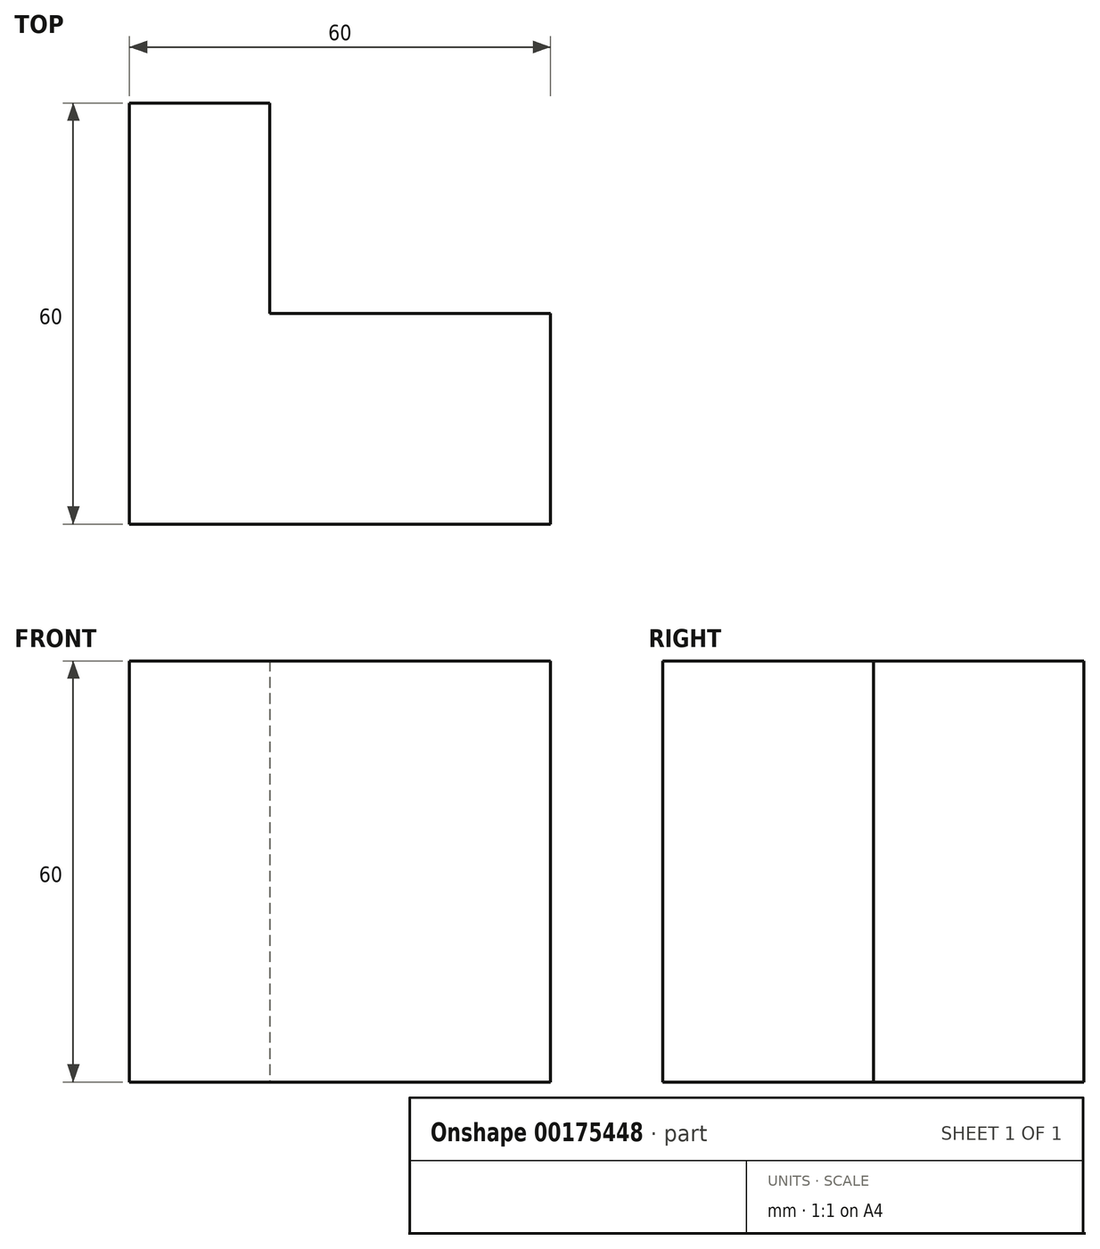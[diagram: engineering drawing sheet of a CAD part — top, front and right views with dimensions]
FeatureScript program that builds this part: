
annotation { "Feature Type Name" : "Feature", "Feature Type Description" : "" }
export const myFeature = defineFeature(function(context is Context, id is Id, definition is map)
    precondition{}
    {
        {
            var Q0;
            Q0=qCreatedBy(makeId("Top.planeOp"),FACE);
            var sketch = newSketch(context, id + "F0", { "sketchPlane" : qUnion([Q0])});
            skLineSegment(sketch, "E0.bottom", {"start": v(-14.12, 16.47) * mm, "end": v(25.88, 16.47) * mm});
            skLineSegment(sketch, "E0.top", {"start": v(-34.12, -13.53) * mm, "end": v(25.88, -13.53) * mm});
            skLineSegment(sketch, "E0.left", {"start": v(-34.12, 16.47) * mm, "end": v(-34.12, -13.53) * mm});
            skLineSegment(sketch, "E0.right", {"start": v(25.88, 16.47) * mm, "end": v(25.88, -13.53) * mm});
            skLineSegment(sketch, "E1.top", {"start": v(-34.12, 46.47) * mm, "end": v(-14.12, 46.47) * mm});
            skLineSegment(sketch, "E1.left", {"start": v(-34.12, 16.47) * mm, "end": v(-34.12, 46.47) * mm});
            skLineSegment(sketch, "E1.right", {"start": v(-14.12, 16.47) * mm, "end": v(-14.12, 46.47) * mm});
            skSolve(sketch);
        }
        {
            var Q0;
            Q0=makeQuery(id+"F0.imprint","IMPRINT",FACE,{"disambiguationData":[TD([[makeQuery(id+"F0.imprint","IMPRINT",EDGE,{"derivedFrom":sQuery(id+"F0.wireOp",EDGE,"E0.bottom")}),-1.0]])]});
            extrude(context, id + "F1", {"entities" : qUnion([Q0]), "depth" : 60 * mm});
        }
    });
